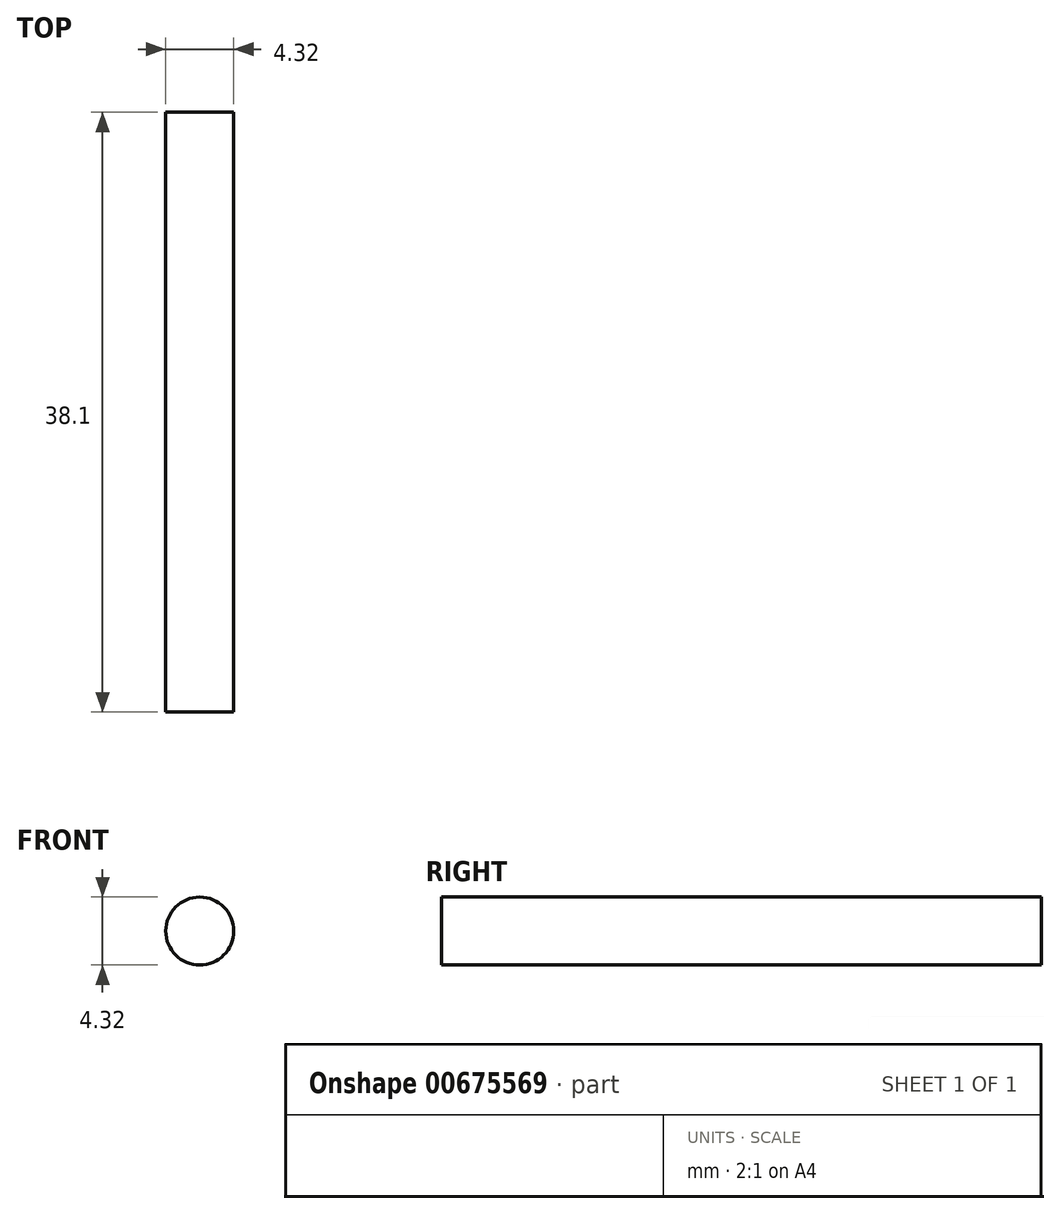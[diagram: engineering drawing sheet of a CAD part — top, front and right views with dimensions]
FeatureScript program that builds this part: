
annotation { "Feature Type Name" : "Feature", "Feature Type Description" : "" }
export const myFeature = defineFeature(function(context is Context, id is Id, definition is map)
    precondition{}
    {
        {
            var Q0;
            Q0=qCreatedBy(makeId("Front.planeOp"),FACE);
            var sketch = newSketch(context, id + "F0", { "sketchPlane" : qUnion([Q0])});
            skCircle(sketch, "E0", {"center": v(-40.77, 4.87) * mm, "radius": 2.16 * mm});
            skSolve(sketch);
        }
        {
            var Q0;
            Q0 = qSketchRegion(id + "F0", true);
            extrude(context, id + "F1", {"entities" : qUnion([Q0]), "depth" : 38.1 * mm, "offsetDistance" : 25.4 * mm});
        }
    });
